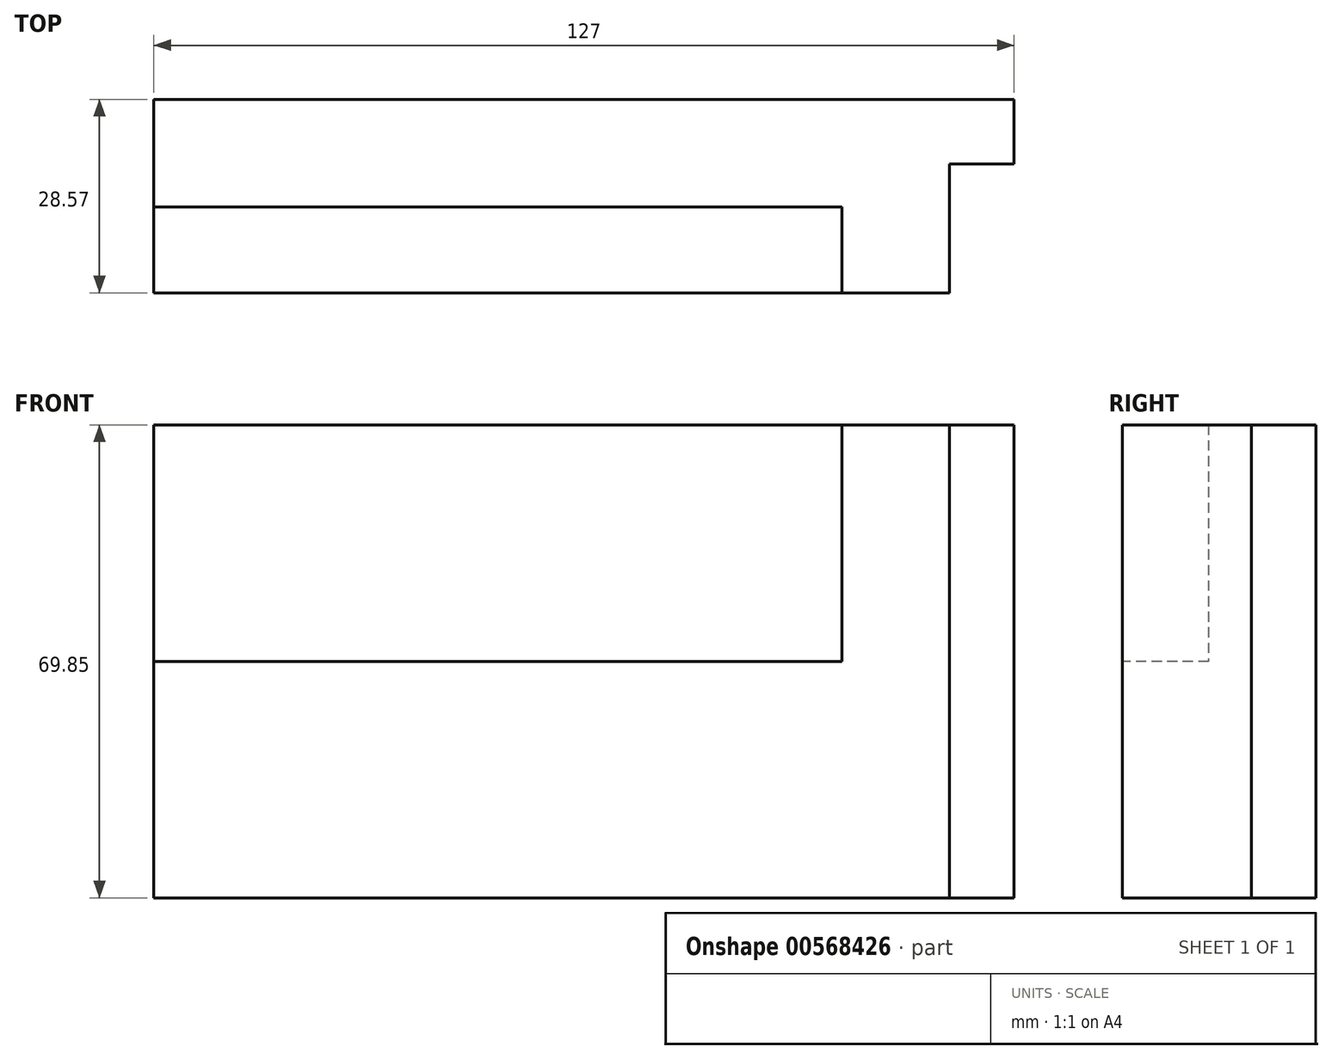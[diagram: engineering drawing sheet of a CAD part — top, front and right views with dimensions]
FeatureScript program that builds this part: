
annotation { "Feature Type Name" : "Feature", "Feature Type Description" : "" }
export const myFeature = defineFeature(function(context is Context, id is Id, definition is map)
    precondition{}
    {
        {
            var Q0;
            Q0=qCreatedBy(makeId("Front.planeOp"),FACE);
            var sketch = newSketch(context, id + "F0", { "sketchPlane" : qUnion([Q0])});
            skLineSegment(sketch, "E0", {"start": v(-38.89, 37.52) * mm, "end": v(-38.89, -32.33) * mm});
            skLineSegment(sketch, "E1", {"start": v(-38.89, -32.33) * mm, "end": v(88.11, -32.33) * mm});
            skLineSegment(sketch, "E2", {"start": v(88.11, -32.33) * mm, "end": v(88.11, 37.52) * mm});
            skLineSegment(sketch, "E3", {"start": v(-38.89, 37.52) * mm, "end": v(88.11, 37.52) * mm});
            skSolve(sketch);
        }
        {
            var Q0;
            Q0 = qSketchRegion(id + "F0", true);
            extrude(context, id + "F1", {"entities" : qUnion([Q0]), "depth" : 28.57 * mm, "offsetDistance" : 25.4 * mm});
        }
        {
            var Q0;
            Q0=makeQuery(id+"F1.opExtrude","CAP_FACE",FACE,{"disambiguationData":[OSD([sQuery(id+"F0.wireOp",EDGE,"E0"),sQuery(id+"F0.wireOp",EDGE,"E1"),sQuery(id+"F0.wireOp",EDGE,"E2"),sQuery(id+"F0.wireOp",EDGE,"E3")])],"isStart":false});
            var sketch = newSketch(context, id + "F2", { "sketchPlane" : qUnion([Q0])});
            skLineSegment(sketch, "E4", {"start": v(62.71, 2.6) * mm, "end": v(-38.89, 2.6) * mm});
            skLineSegment(sketch, "E5", {"start": v(-38.89, 2.6) * mm, "end": v(-38.89, 37.52) * mm});
            skLineSegment(sketch, "E6", {"start": v(62.71, 2.6) * mm, "end": v(62.71, 37.52) * mm});
            skSolve(sketch);
        }
        {
            var Q0;
            Q0=makeQuery(id+"F2.imprint","IMPRINT",FACE,{"disambiguationData":[TD([[makeQuery(id+"F2.imprint","IMPRINT",EDGE,{"derivedFrom":sQuery(id+"F2.wireOp",EDGE,"E4")}),-1.0]])]});
            extrude(context, id + "F3", {"entities" : qUnion([Q0]), "operationType" : NewBodyOperationType.REMOVE, "oppositeDirection" : true, "depth" : 12.7 * mm, "offsetDistance" : 25.4 * mm});
        }
        {
            var Q0;
            Q0=makeQuery(id+"F1.opExtrude","CAP_FACE",FACE,{"disambiguationData":[OSD([sQuery(id+"F0.wireOp",EDGE,"E0"),sQuery(id+"F0.wireOp",EDGE,"E1"),sQuery(id+"F0.wireOp",EDGE,"E2"),sQuery(id+"F0.wireOp",EDGE,"E3")])],"isStart":false});
            var sketch = newSketch(context, id + "F4", { "sketchPlane" : qUnion([Q0])});
            skLineSegment(sketch, "E7", {"start": v(78.59, 37.52) * mm, "end": v(78.59, -32.33) * mm});
            skLineSegment(sketch, "E8", {"start": v(78.59, -32.33) * mm, "end": v(88.11, -32.33) * mm});
            skSolve(sketch);
        }
        {
            var Q0;
            {var subQ0=sQuery(id+"F4.wireOp",EDGE,"E7");Q0=makeQuery(id+"F4.imprint","IMPRINT",FACE,{"disambiguationData":[TD([[makeQuery(id+"F4.imprint","IMPRINT",EDGE,{"derivedFrom":subQ0}),1.0]])]});}
            extrude(context, id + "F5", {"entities" : qUnion([Q0]), "operationType" : NewBodyOperationType.REMOVE, "oppositeDirection" : true, "depth" : 19.05 * mm, "offsetDistance" : 25.4 * mm});
        }
    });
